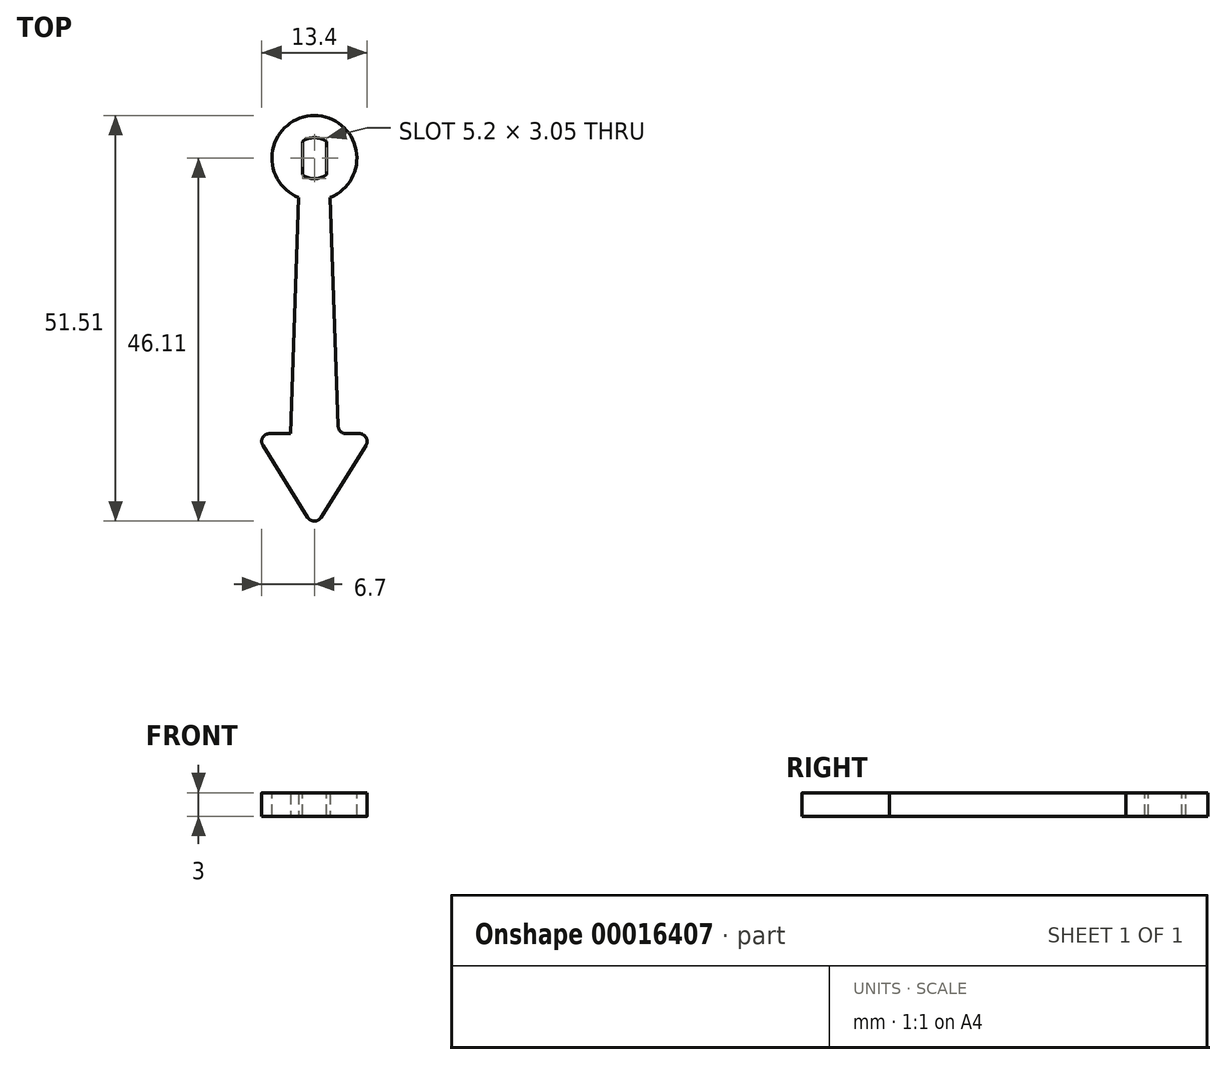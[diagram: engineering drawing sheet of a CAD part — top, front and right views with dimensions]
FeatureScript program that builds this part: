
annotation { "Feature Type Name" : "Feature", "Feature Type Description" : "" }
export const myFeature = defineFeature(function(context is Context, id is Id, definition is map)
    precondition{}
    {
        {
            var Q0;
            Q0=qCreatedBy(makeId("Top.planeOp"),FACE);
            var sketch = newSketch(context, id + "F0", { "sketchPlane" : qUnion([Q0])});
            skArc(sketch, "E0", {"start": v(-1.53, -2.1) * mm, "mid": v(0, -2.6) * mm, "end": v(1.52, -2.1) * mm});
            skCircle(sketch, "E1", {"center": v(0, 0) * mm, "radius": 5.4 * mm});
            skLineSegment(sketch, "E2", {"start": v(-1.53, 2.1) * mm, "end": v(-1.52, -2.1) * mm});
            skLineSegment(sketch, "E3", {"start": v(1.52, 2.1) * mm, "end": v(1.53, -2.1) * mm});
            skArc(sketch, "E4.trimOffspring", {"start": v(1.53, 2.1) * mm, "mid": v(0, 2.6) * mm, "end": v(-1.53, 2.1) * mm});
            skSolve(sketch);
        }
        {
            var Q0;
            Q0 = qSketchRegion(id + "F0", true);
            extrude(context, id + "F1", {"entities" : qUnion([Q0]), "endBound" : BoundingType.SYMMETRIC, "oppositeDirection" : true, "depth" : 3 * mm});
        }
        {
            var Q0;
            Q0=makeQuery(id+"F1.opExtrude","CAP_FACE",FACE,{"disambiguationData":[OSD([sQuery(id+"F0.wireOp",EDGE,"E0"),sQuery(id+"F0.wireOp",EDGE,"E1"),sQuery(id+"F0.wireOp",EDGE,"E2"),sQuery(id+"F0.wireOp",EDGE,"E3"),sQuery(id+"F0.wireOp",EDGE,"E4.trimOffspring")])],"isStart":false});
            var sketch = newSketch(context, id + "F2", { "sketchPlane" : qUnion([Q0])});
            skLineSegment(sketch, "E5", {"start": v(0, 0) * mm, "end": v(0, 35) * mm, "construction": true});
            skLineSegment(sketch, "E6", {"start": v(-29.97, 35) * mm, "end": v(29.97, 35) * mm});
            skLineSegment(sketch, "E7", {"start": v(-2, 5.02) * mm, "end": v(2, 5.02) * mm});
            skLineSegment(sketch, "E8", {"start": v(2, 5.02) * mm, "end": v(3.05, 35) * mm});
            skLineSegment(sketch, "E9", {"start": v(-3.05, 35) * mm, "end": v(-2, 5.02) * mm});
            skSolve(sketch);
        }
        {
            var Q0;
            {var subQ2=sQuery(id+"F2.wireOp",EDGE,"E8");Q0=makeQuery(id+"F2.imprint","IMPRINT",FACE,{"disambiguationData":[TD([[makeQuery(id+"F2.imprint","IMPRINT",EDGE,{"derivedFrom":subQ2}),1.0]])]});}
            extrude(context, id + "F3", {"entities" : qUnion([Q0]), "operationType" : NewBodyOperationType.ADD, "oppositeDirection" : true, "depth" : 3 * mm});
        }
        {
            var Q0;
            Q0=makeQuery(id+"F3.opExtrude","CAP_FACE",FACE,{"disambiguationData":[OSD([sQuery(id+"F0.wireOp",EDGE,"E1"),sQuery(id+"F2.wireOp",EDGE,"E6"),sQuery(id+"F2.wireOp",EDGE,"E8"),sQuery(id+"F2.wireOp",EDGE,"E9")])],"isStart":true});
            var sketch = newSketch(context, id + "F4", { "sketchPlane" : qUnion([Q0])});
            skLineSegment(sketch, "E10", {"start": v(0, 35) * mm, "end": v(0, 47) * mm});
            skLineSegment(sketch, "E11", {"start": v(-7.5, 35) * mm, "end": v(7.5, 35) * mm});
            skLineSegment(sketch, "E12", {"start": v(-7.5, 35) * mm, "end": v(0, 47) * mm});
            skLineSegment(sketch, "E13", {"start": v(7.5, 35) * mm, "end": v(0, 47) * mm});
            skSolve(sketch);
        }
        {
            var Q0;
            {var subQ3=sQuery(id+"F4.wireOp",EDGE,"E10");Q0=makeQuery(id+"F4.imprint","IMPRINT",FACE,{"disambiguationData":[TD([[makeQuery(id+"F4.imprint","IMPRINT",EDGE,{"derivedFrom":subQ3}),1.0]])]});}
            var Q1;
            {var subQ3=sQuery(id+"F4.wireOp",EDGE,"E10");Q1=makeQuery(id+"F4.imprint","IMPRINT",FACE,{"disambiguationData":[TD([[makeQuery(id+"F4.imprint","IMPRINT",EDGE,{"derivedFrom":subQ3}),-1.0]])]});}
            var Q2;
            Q2=makeQuery(id+"F3.opExtrude","CAP_FACE",FACE,{"disambiguationData":[OSD([sQuery(id+"F0.wireOp",EDGE,"E1"),sQuery(id+"F2.wireOp",EDGE,"E6"),sQuery(id+"F2.wireOp",EDGE,"E8"),sQuery(id+"F2.wireOp",EDGE,"E9")])],"isStart":false});
            extrude(context, id + "F5", {"entities" : qUnion([Q0, Q1]), "operationType" : NewBodyOperationType.ADD, "endBound" : BoundingType.UP_TO_SURFACE, "oppositeDirection" : true, "endBoundEntityFace" : qUnion([Q2]), "depth" : 1 * mm});
        }
        {
            var Q0;
            Q0=makeQuery(id+"F5.opExtrude","SWEPT_EDGE",EDGE,{"disambiguationData":[OSD([sQuery(id+"F4.wireOp",EDGE,"E11"),sQuery(id+"F4.wireOp",EDGE,"E12")])]});
            var Q1;
            Q1=makeQuery(id+"F5.opExtrude","SWEPT_EDGE",EDGE,{"disambiguationData":[OSD([sQuery(id+"F4.wireOp",EDGE,"E10"),sQuery(id+"F4.wireOp",EDGE,"E12"),sQuery(id+"F4.wireOp",EDGE,"E13")])]});
            var Q2;
            Q2=makeQuery(id+"F3.opExtrude","SWEPT_EDGE",EDGE,{"disambiguationData":[OSD([sQuery(id+"F2.wireOp",EDGE,"E6"),sQuery(id+"F2.wireOp",EDGE,"E8")])]});
            var Q3;
            Q3=makeQuery(id+"F3.opExtrude","SWEPT_EDGE",EDGE,{"disambiguationData":[OSD([sQuery(id+"F2.wireOp",EDGE,"E6"),sQuery(id+"F2.wireOp",EDGE,"E9")])]});
            var Q4;
            Q4=makeQuery(id+"F5.opExtrude","SWEPT_EDGE",EDGE,{"disambiguationData":[OSD([sQuery(id+"F4.wireOp",EDGE,"E11"),sQuery(id+"F4.wireOp",EDGE,"E13")])]});
            fillet(context, id + "F6", {"entities" : qUnion([Q0, Q1, Q2, Q3, Q4]), "radius" : 1 * mm, "tangentPropagation" : true, "allowEdgeOverflow" : false});
        }
    });
